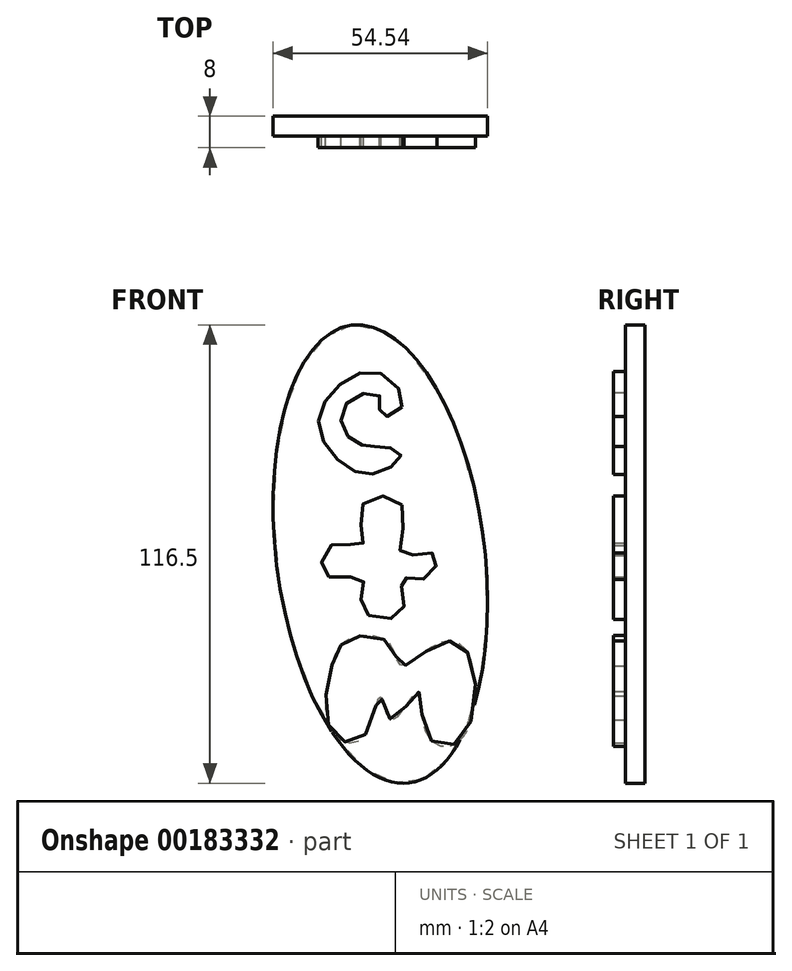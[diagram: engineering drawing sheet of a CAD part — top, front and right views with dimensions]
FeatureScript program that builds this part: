
annotation { "Feature Type Name" : "Feature", "Feature Type Description" : "" }
export const myFeature = defineFeature(function(context is Context, id is Id, definition is map)
    precondition{}
    {
        {
            var Q0;
            Q0=qCreatedBy(makeId("Front.planeOp"),FACE);
            var sketch = newSketch(context, id + "F0", { "sketchPlane" : qUnion([Q0])});
            skEllipse(sketch, "E0", {"center": v(0, 0) * mm, "majorRadius": 58.6 * mm, "minorRadius": 26.48 * mm, "majorAxis": v(-0.12, 1)});
            skSolve(sketch);
        }
        {
            var Q0;
            Q0 = qSketchRegion(id + "F0", true);
            extrude(context, id + "F1", {"entities" : qUnion([Q0]), "depth" : 5 * mm});
        }
        {
            var Q0;
            Q0=makeQuery(id+"F1.opExtrude","CAP_FACE",FACE,{"disambiguationData":[OSD([sQuery(id+"F0.wireOp",EDGE,"E0")])],"isStart":false});
            var sketch = newSketch(context, id + "F2", { "sketchPlane" : qUnion([Q0])});
            skFitSpline(sketch, "E1", {"points": [v(5.44, 37.36) * mm, v(0, 45.94) * mm, v(-11.14, 42.22) * mm, v(-15.71, 32.21) * mm, v(-8.28, 21.92) * mm, v(0, 20.78) * mm, v(5.16, 25.35) * mm, v(0, 27.35) * mm, v(-4.56, 27.64) * mm, v(-9.7, 32.21) * mm, v(-7.14, 39.65) * mm, v(0, 39.93) * mm, v(0, 35.36) * mm, v(5.44, 37.36) * mm]});
            skFitSpline(sketch, "E2", {"points": [v(5.44, 12.49) * mm, v(-4.56, 12.49) * mm, v(-4.56, 2.48) * mm, v(-12, 2.48) * mm, v(-14, -5.24) * mm, v(-4.56, -6.38) * mm, v(-4.56, -14.1) * mm, v(5.44, -14.96) * mm, v(5.44, -6.38) * mm, v(11.73, -6.1) * mm, v(13.73, 0) * mm, v(5.44, 0) * mm, v(5.44, 12.49) * mm]});
            skFitSpline(sketch, "E3", {"points": [v(-12.28, -28.1) * mm, v(-12.44, -45.01) * mm, v(-4.56, -46.7) * mm, v(0, -36.11) * mm, v(2.87, -42.12) * mm, v(9.45, -34.97) * mm, v(11.73, -45.83) * mm, v(20.27, -47.26) * mm, v(22.6, -25.82) * mm, v(14.88, -22.68) * mm, v(5.44, -28.4) * mm, v(2.3, -22.68) * mm, v(-7.7, -21.53) * mm, v(-12.28, -28.1) * mm]});
            skSolve(sketch);
        }
        {
            var Q0;
            Q0 = qSketchRegion(id + "F2", true);
            extrude(context, id + "F3", {"entities" : qUnion([Q0]), "operationType" : NewBodyOperationType.ADD, "depth" : 3 * mm});
        }
    });
